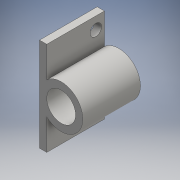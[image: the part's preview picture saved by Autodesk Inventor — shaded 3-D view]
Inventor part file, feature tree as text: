
AUTODESK INVENTOR PART (.ipt)
format: ipt  version: 2016 (Build 200138000, 138)  size: 117,248 bytes
history: native  units: mm
features: extrude x2, sketch x2
ambient origin geometry x8: Origin, YZ Plane, XZ Plane, XY Plane, X Axis, Y Axis, Z Axis, Center Point
bodies: Solid1 (feature_tree)
feature tree (4):
  extrude  "Extrusion1"  Depth=26.0mm
  extrude  "Extrusion2"  Depth=16.0mm TaperAngle=0.0deg
  sketch  "Sketch1"  dims[d0=8.0mm d2=26.0mm]
  sketch  "Sketch2"  dims[d3=2.0mm d4=16.0mm d5=0.0mm d10=3.2mm d11=3.2mm d12=16.0mm d13=0.0mm d14=2.4mm d15=2.4mm]
